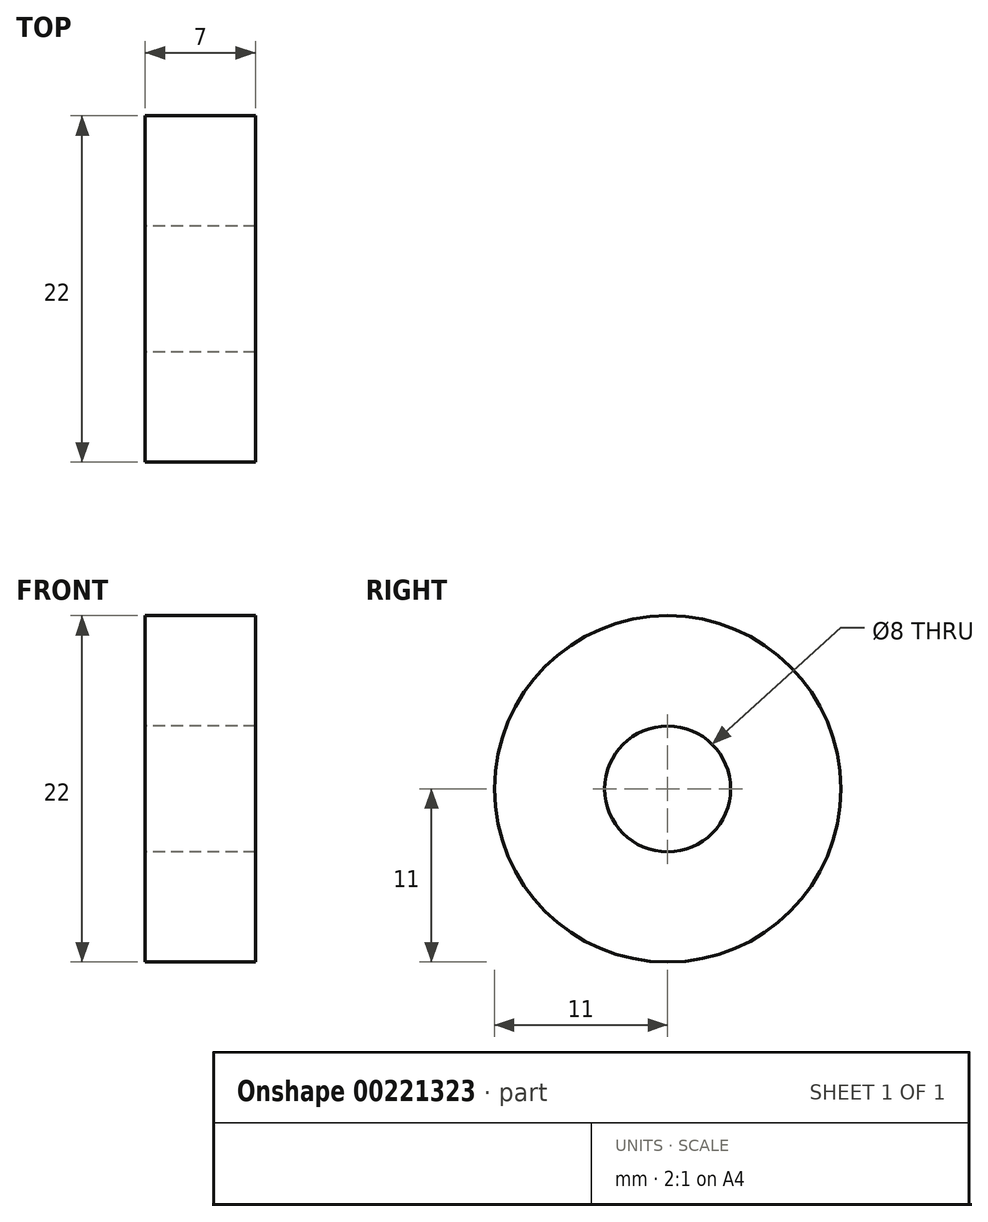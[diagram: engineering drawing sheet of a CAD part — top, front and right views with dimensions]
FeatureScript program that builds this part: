
annotation { "Feature Type Name" : "Feature", "Feature Type Description" : "" }
export const myFeature = defineFeature(function(context is Context, id is Id, definition is map)
    precondition{}
    {
        {
            var Q0;
            Q0=qCreatedBy(makeId("Right.planeOp"),FACE);
            var sketch = newSketch(context, id + "F0", { "sketchPlane" : qUnion([Q0])});
            skCircle(sketch, "E0", {"center": v(0, 0) * mm, "radius": 4 * mm});
            skCircle(sketch, "E1", {"center": v(0, 0) * mm, "radius": 11 * mm});
            skSolve(sketch);
        }
        {
            var Q0;
            Q0 = qSketchRegion(id + "F0", true);
            extrude(context, id + "F1", {"entities" : qUnion([Q0]), "depth" : 7 * mm});
        }
    });
